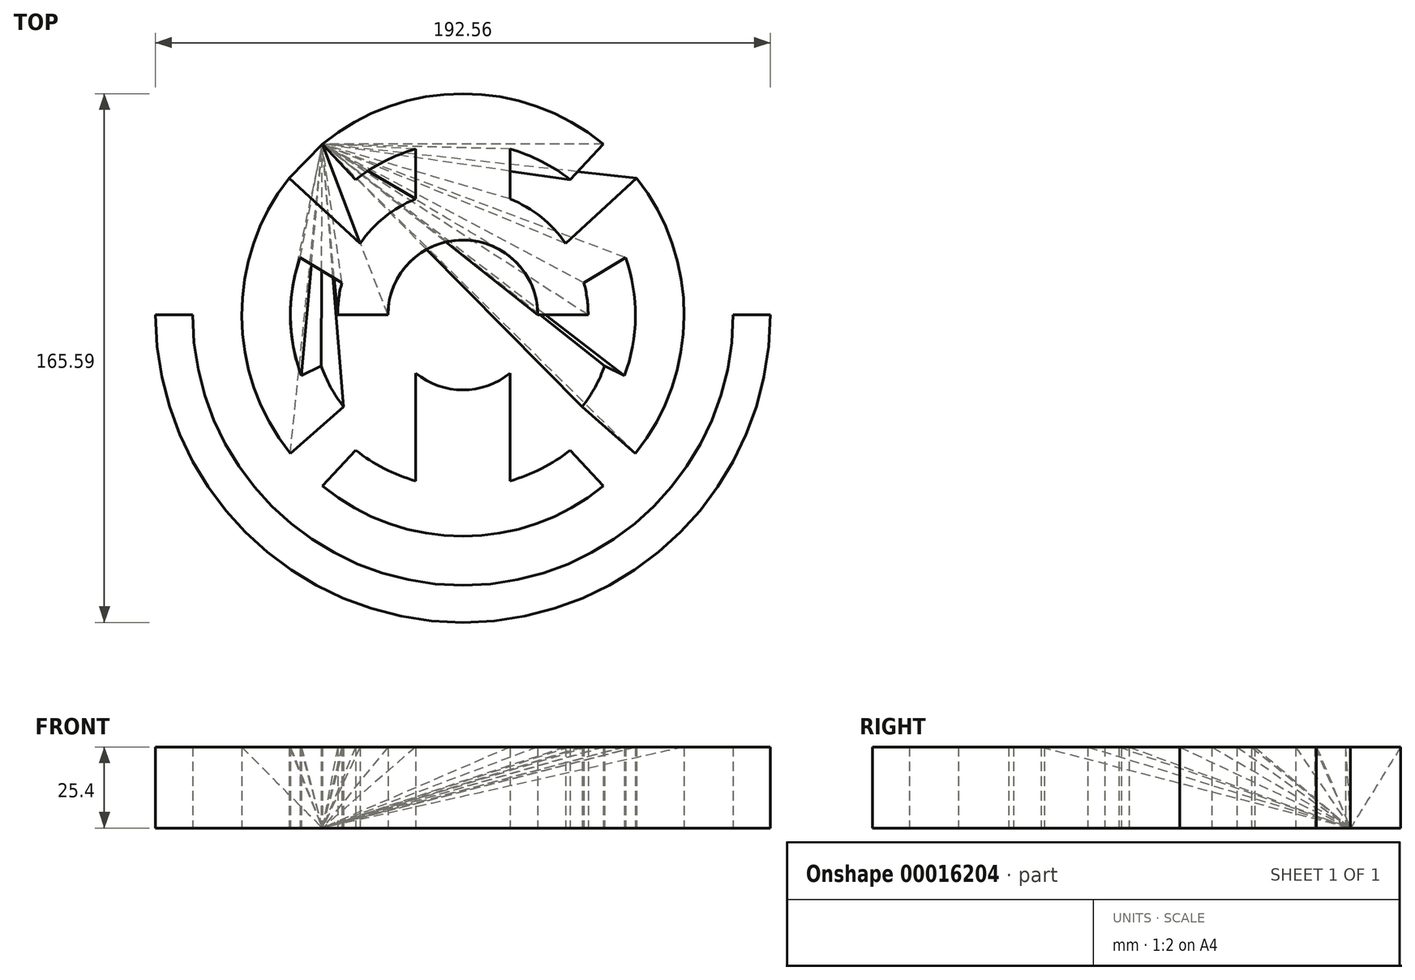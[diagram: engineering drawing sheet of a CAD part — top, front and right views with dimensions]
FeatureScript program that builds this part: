
annotation { "Feature Type Name" : "Feature", "Feature Type Description" : "" }
export const myFeature = defineFeature(function(context is Context, id is Id, definition is map)
    precondition{}
    {
        {
            var Q0;
            Q0=qCreatedBy(makeId("Top.planeOp"),FACE);
            var sketch = newSketch(context, id + "F0", { "sketchPlane" : qUnion([Q0])});
            skCircle(sketch, "E0", {"center": v(0, 0) * mm, "radius": 96.28 * mm});
            skCircle(sketch, "E1", {"center": v(0, 0) * mm, "radius": 84.65 * mm});
            skCircle(sketch, "E2", {"center": v(0, 0) * mm, "radius": 23.48 * mm});
            skCircle(sketch, "E3", {"center": v(0, 0) * mm, "radius": 39.24 * mm});
            skCircle(sketch, "E4", {"center": v(0, 0) * mm, "radius": 69.3 * mm});
            skCircle(sketch, "E5", {"center": v(0, 0) * mm, "radius": 54.05 * mm});
            skLineSegment(sketch, "E6", {"start": v(14.83, 67.7) * mm, "end": v(14.83, -51.98) * mm});
            skLineSegment(sketch, "E7", {"start": v(0, 69.3) * mm, "end": v(0, -96.28) * mm});
            skLineSegment(sketch, "E8.MirrorCS", {"start": v(-14.83, 67.7) * mm, "end": v(-14.83, -51.98) * mm});
            skLineSegment(sketch, "E9", {"start": v(96.28, 0) * mm, "end": v(-96.28, 0) * mm});
            skLineSegment(sketch, "E10", {"start": v(33.56, -42.37) * mm, "end": v(44.04, -53.52) * mm});
            skLineSegment(sketch, "E11.MirrorCS", {"start": v(-33.56, -42.37) * mm, "end": v(-44.04, -53.52) * mm});
            skLineSegment(sketch, "E12.MirrorCS", {"start": v(33.56, 42.37) * mm, "end": v(44.04, 53.52) * mm});
            skLineSegment(sketch, "E13.MirrorCS", {"start": v(-33.56, 42.37) * mm, "end": v(-44.04, 53.52) * mm});
            skCircle(sketch, "E14", {"center": v(0, 0) * mm, "radius": 47.19 * mm});
            skLineSegment(sketch, "E15", {"start": v(32.19, 22.45) * mm, "end": v(54.44, 42.9) * mm});
            skLineSegment(sketch, "E16", {"start": v(54.08, -43.34) * mm, "end": v(37.38, -28.8) * mm});
            skLineSegment(sketch, "E17", {"start": v(64.28, -25.92) * mm, "end": v(44.43, -15.9) * mm});
            skLineSegment(sketch, "E18", {"start": v(37.92, 10.11) * mm, "end": v(64.25, 25.99) * mm});
            skLineSegment(sketch, "E19.MirrorCS", {"start": v(-32.19, 22.45) * mm, "end": v(-54.44, 42.9) * mm});
            skLineSegment(sketch, "E20.MirrorCS", {"start": v(-37.92, 10.11) * mm, "end": v(-64.25, 25.99) * mm});
            skLineSegment(sketch, "E21.MirrorCS", {"start": v(-64.28, -25.92) * mm, "end": v(-44.43, -15.9) * mm});
            skLineSegment(sketch, "E22.MirrorCS", {"start": v(-54.08, -43.34) * mm, "end": v(-37.38, -28.8) * mm});
            skSolve(sketch);
        }
        {
            var Q0;
            {var subQ3=sQuery(id+"F0.wireOp",EDGE,"E3");var subQ5=sQuery(id+"F0.wireOp",EDGE,"E15");var subQ7=makeQuery(id+"F0.imprint","INTERSECT",VERTEX,{"derivedFrom":[subQ3,subQ5]});Q0=makeQuery(id+"F0.imprint","IMPRINT",FACE,{"disambiguationData":[TD([[makeQuery(id+"F0.imprint","IMPRINT",EDGE,{"disambiguationData":[TD([[subQ7,1.0]])],"derivedFrom":subQ3}),-1.0]])]});}
            var Q1;
            {var subQ3=sQuery(id+"F0.wireOp",EDGE,"E2");var subQ5=sQuery(id+"F0.wireOp",EDGE,"E6");var subQ7=makeQuery(id+"F0.imprint","INTERSECT",VERTEX,{"disambiguationData":[OD(0.0)],"derivedFrom":[subQ3,subQ5]});Q1=makeQuery(id+"F0.imprint","IMPRINT",FACE,{"disambiguationData":[TD([[makeQuery(id+"F0.imprint","IMPRINT",EDGE,{"disambiguationData":[TD([[subQ7,-1.0]])],"derivedFrom":subQ3}),-1.0]])]});}
            var Q2;
            {var subQ3=sQuery(id+"F0.wireOp",EDGE,"E4");var subQ5=sQuery(id+"F0.wireOp",EDGE,"E6");var subQ7=makeQuery(id+"F0.imprint","INTERSECT",VERTEX,{"derivedFrom":[subQ3,subQ5]});Q2=makeQuery(id+"F0.imprint","IMPRINT",FACE,{"disambiguationData":[TD([[makeQuery(id+"F0.imprint","IMPRINT",EDGE,{"disambiguationData":[TD([[subQ7,-1.0]])],"derivedFrom":subQ3}),1.0]])]});}
            var Q3;
            {var subQ0=sQuery(id+"F0.wireOp",EDGE,"E18");var subQ3=sQuery(id+"F0.wireOp",EDGE,"E4");var subQ4=makeQuery(id+"F0.imprint","INTERSECT",VERTEX,{"derivedFrom":[subQ3,subQ0]});Q3=makeQuery(id+"F0.imprint","IMPRINT",FACE,{"disambiguationData":[TD([[makeQuery(id+"F0.imprint","IMPRINT",EDGE,{"disambiguationData":[TD([[subQ4,1.0]])],"derivedFrom":subQ3}),1.0]])]});}
            var Q4;
            {var subQ0=sQuery(id+"F0.wireOp",EDGE,"E11.MirrorCS");Q4=makeQuery(id+"F0.imprint","IMPRINT",FACE,{"disambiguationData":[TD([[makeQuery(id+"F0.imprint","IMPRINT",EDGE,{"derivedFrom":subQ0}),1.0]])]});}
            var Q5;
            {var subQ3=sQuery(id+"F0.wireOp",EDGE,"E7");var subQ5=sQuery(id+"F0.wireOp",EDGE,"E5");var subQ7=makeQuery(id+"F0.imprint","INTERSECT",VERTEX,{"disambiguationData":[OD(0.0)],"derivedFrom":[subQ5,subQ3]});Q5=makeQuery(id+"F0.imprint","IMPRINT",FACE,{"disambiguationData":[TD([[makeQuery(id+"F0.imprint","IMPRINT",EDGE,{"disambiguationData":[TD([[subQ7,-1.0]])],"derivedFrom":subQ5}),1.0]])]});}
            var Q6;
            {var subQ3=sQuery(id+"F0.wireOp",EDGE,"E2");var subQ5=sQuery(id+"F0.wireOp",EDGE,"E7");var subQ7=makeQuery(id+"F0.imprint","INTERSECT",VERTEX,{"disambiguationData":[OD(1.0)],"derivedFrom":[subQ3,subQ5]});Q6=makeQuery(id+"F0.imprint","IMPRINT",FACE,{"disambiguationData":[TD([[makeQuery(id+"F0.imprint","IMPRINT",EDGE,{"disambiguationData":[TD([[subQ7,-1.0]])],"derivedFrom":subQ3}),-1.0]])]});}
            var Q7;
            {var subQ0=sQuery(id+"F0.wireOp",EDGE,"E8.MirrorCS");var subQ3=sQuery(id+"F0.wireOp",EDGE,"E2");var subQ4=makeQuery(id+"F0.imprint","INTERSECT",VERTEX,{"disambiguationData":[OD(1.0)],"derivedFrom":[subQ3,subQ0]});Q7=makeQuery(id+"F0.imprint","IMPRINT",FACE,{"disambiguationData":[TD([[makeQuery(id+"F0.imprint","IMPRINT",EDGE,{"disambiguationData":[TD([[subQ4,-1.0]])],"derivedFrom":subQ3}),-1.0]])]});}
            var Q8;
            {var subQ0=sQuery(id+"F0.wireOp",EDGE,"E12.MirrorCS");Q8=makeQuery(id+"F0.imprint","IMPRINT",FACE,{"disambiguationData":[TD([[makeQuery(id+"F0.imprint","IMPRINT",EDGE,{"derivedFrom":subQ0}),1.0]])]});}
            var Q9;
            {var subQ3=sQuery(id+"F0.wireOp",EDGE,"E4");var subQ5=sQuery(id+"F0.wireOp",EDGE,"E7");var subQ7=makeQuery(id+"F0.imprint","INTERSECT",VERTEX,{"disambiguationData":[OD(0.0)],"derivedFrom":[subQ3,subQ5]});Q9=makeQuery(id+"F0.imprint","IMPRINT",FACE,{"disambiguationData":[TD([[makeQuery(id+"F0.imprint","IMPRINT",EDGE,{"disambiguationData":[TD([[subQ7,-1.0]])],"derivedFrom":subQ3}),1.0]])]});}
            var Q10;
            {var subQ3=sQuery(id+"F0.wireOp",EDGE,"E4");var subQ5=sQuery(id+"F0.wireOp",EDGE,"E16");var subQ7=makeQuery(id+"F0.imprint","INTERSECT",VERTEX,{"derivedFrom":[subQ3,subQ5]});Q10=makeQuery(id+"F0.imprint","IMPRINT",FACE,{"disambiguationData":[TD([[makeQuery(id+"F0.imprint","IMPRINT",EDGE,{"disambiguationData":[TD([[subQ7,-1.0]])],"derivedFrom":subQ3}),1.0]])]});}
            var Q11;
            {var subQ0=sQuery(id+"F0.wireOp",EDGE,"E17");var subQ3=sQuery(id+"F0.wireOp",EDGE,"E4");var subQ4=makeQuery(id+"F0.imprint","INTERSECT",VERTEX,{"derivedFrom":[subQ3,subQ0]});Q11=makeQuery(id+"F0.imprint","IMPRINT",FACE,{"disambiguationData":[TD([[makeQuery(id+"F0.imprint","IMPRINT",EDGE,{"disambiguationData":[TD([[subQ4,-1.0]])],"derivedFrom":subQ3}),1.0]])]});}
            var Q12;
            {var subQ3=sQuery(id+"F0.wireOp",EDGE,"E0");var subQ5=sQuery(id+"F0.wireOp",EDGE,"E7");var subQ7=makeQuery(id+"F0.imprint","INTERSECT",VERTEX,{"derivedFrom":[subQ3,subQ5]});Q12=makeQuery(id+"F0.imprint","IMPRINT",FACE,{"disambiguationData":[TD([[makeQuery(id+"F0.imprint","IMPRINT",EDGE,{"disambiguationData":[TD([[subQ7,-1.0]])],"derivedFrom":subQ3}),1.0]])]});}
            var Q13;
            {var subQ0=sQuery(id+"F0.wireOp",EDGE,"E20.MirrorCS");var subQ3=sQuery(id+"F0.wireOp",EDGE,"E4");var subQ4=makeQuery(id+"F0.imprint","INTERSECT",VERTEX,{"derivedFrom":[subQ3,subQ0]});Q13=makeQuery(id+"F0.imprint","IMPRINT",FACE,{"disambiguationData":[TD([[makeQuery(id+"F0.imprint","IMPRINT",EDGE,{"disambiguationData":[TD([[subQ4,-1.0]])],"derivedFrom":subQ3}),1.0]])]});}
            var Q14;
            {var subQ3=sQuery(id+"F0.wireOp",EDGE,"E4");var subQ5=sQuery(id+"F0.wireOp",EDGE,"E21.MirrorCS");var subQ7=makeQuery(id+"F0.imprint","INTERSECT",VERTEX,{"derivedFrom":[subQ3,subQ5]});Q14=makeQuery(id+"F0.imprint","IMPRINT",FACE,{"disambiguationData":[TD([[makeQuery(id+"F0.imprint","IMPRINT",EDGE,{"disambiguationData":[TD([[subQ7,-1.0]])],"derivedFrom":subQ3}),1.0]])]});}
            var Q15;
            {var subQ3=sQuery(id+"F0.wireOp",EDGE,"E0");var subQ5=sQuery(id+"F0.wireOp",EDGE,"E7");var subQ7=makeQuery(id+"F0.imprint","INTERSECT",VERTEX,{"derivedFrom":[subQ3,subQ5]});Q15=makeQuery(id+"F0.imprint","IMPRINT",FACE,{"disambiguationData":[TD([[makeQuery(id+"F0.imprint","IMPRINT",EDGE,{"disambiguationData":[TD([[subQ7,1.0]])],"derivedFrom":subQ3}),1.0]])]});}
            var Q16;
            {var subQ1=sQuery(id+"F0.wireOp",EDGE,"E5");var subQ5=sQuery(id+"F0.wireOp",EDGE,"E16");var subQ6=makeQuery(id+"F0.imprint","INTERSECT",VERTEX,{"derivedFrom":[subQ1,subQ5]});Q16=makeQuery(id+"F0.imprint","IMPRINT",FACE,{"disambiguationData":[TD([[makeQuery(id+"F0.imprint","IMPRINT",EDGE,{"disambiguationData":[TD([[subQ6,-1.0]])],"derivedFrom":subQ1}),1.0]])]});}
            var Q17;
            {var subQ3=sQuery(id+"F0.wireOp",EDGE,"E4");var subQ5=sQuery(id+"F0.wireOp",EDGE,"E15");var subQ7=makeQuery(id+"F0.imprint","INTERSECT",VERTEX,{"derivedFrom":[subQ3,subQ5]});Q17=makeQuery(id+"F0.imprint","IMPRINT",FACE,{"disambiguationData":[TD([[makeQuery(id+"F0.imprint","IMPRINT",EDGE,{"disambiguationData":[TD([[subQ7,1.0]])],"derivedFrom":subQ3}),1.0]])]});}
            var Q18;
            {var subQ3=sQuery(id+"F0.wireOp",EDGE,"E7");var subQ5=sQuery(id+"F0.wireOp",EDGE,"E3");var subQ7=makeQuery(id+"F0.imprint","INTERSECT",VERTEX,{"disambiguationData":[OD(0.0)],"derivedFrom":[subQ5,subQ3]});Q18=makeQuery(id+"F0.imprint","IMPRINT",FACE,{"disambiguationData":[TD([[makeQuery(id+"F0.imprint","IMPRINT",EDGE,{"disambiguationData":[TD([[subQ7,-1.0]])],"derivedFrom":subQ5}),-1.0]])]});}
            var Q19;
            {var subQ0=sQuery(id+"F0.wireOp",EDGE,"E19.MirrorCS");var subQ3=sQuery(id+"F0.wireOp",EDGE,"E4");var subQ4=makeQuery(id+"F0.imprint","INTERSECT",VERTEX,{"derivedFrom":[subQ3,subQ0]});Q19=makeQuery(id+"F0.imprint","IMPRINT",FACE,{"disambiguationData":[TD([[makeQuery(id+"F0.imprint","IMPRINT",EDGE,{"disambiguationData":[TD([[subQ4,-1.0]])],"derivedFrom":subQ3}),1.0]])]});}
            var Q20;
            {var subQ1=sQuery(id+"F0.wireOp",EDGE,"E8.MirrorCS");var subQ5=sQuery(id+"F0.wireOp",EDGE,"E5");var subQ6=makeQuery(id+"F0.imprint","INTERSECT",VERTEX,{"disambiguationData":[OD(0.0)],"derivedFrom":[subQ5,subQ1]});Q20=makeQuery(id+"F0.imprint","IMPRINT",FACE,{"disambiguationData":[TD([[makeQuery(id+"F0.imprint","IMPRINT",EDGE,{"disambiguationData":[TD([[subQ6,-1.0]])],"derivedFrom":subQ5}),1.0]])]});}
            var Q21;
            {var subQ0=sQuery(id+"F0.wireOp",EDGE,"E21.MirrorCS");var subQ3=sQuery(id+"F0.wireOp",EDGE,"E4");var subQ4=makeQuery(id+"F0.imprint","INTERSECT",VERTEX,{"derivedFrom":[subQ3,subQ0]});Q21=makeQuery(id+"F0.imprint","IMPRINT",FACE,{"disambiguationData":[TD([[makeQuery(id+"F0.imprint","IMPRINT",EDGE,{"disambiguationData":[TD([[subQ4,1.0]])],"derivedFrom":subQ3}),1.0]])]});}
            var Q22;
            {var subQ0=sQuery(id+"F0.wireOp",EDGE,"E9");var subQ3=sQuery(id+"F0.wireOp",EDGE,"E2");var subQ4=makeQuery(id+"F0.imprint","INTERSECT",VERTEX,{"disambiguationData":[OD(1.0)],"derivedFrom":[subQ3,subQ0]});Q22=makeQuery(id+"F0.imprint","IMPRINT",FACE,{"disambiguationData":[TD([[makeQuery(id+"F0.imprint","IMPRINT",EDGE,{"disambiguationData":[TD([[subQ4,-1.0]])],"derivedFrom":subQ3}),-1.0]])]});}
            var Q23;
            {var subQ1=sQuery(id+"F0.wireOp",EDGE,"E8.MirrorCS");var subQ5=sQuery(id+"F0.wireOp",EDGE,"E3");var subQ6=makeQuery(id+"F0.imprint","INTERSECT",VERTEX,{"disambiguationData":[OD(1.0)],"derivedFrom":[subQ5,subQ1]});Q23=makeQuery(id+"F0.imprint","IMPRINT",FACE,{"disambiguationData":[TD([[makeQuery(id+"F0.imprint","IMPRINT",EDGE,{"disambiguationData":[TD([[subQ6,-1.0]])],"derivedFrom":subQ5}),-1.0]])]});}
            var Q24;
            {var subQ0=sQuery(id+"F0.wireOp",EDGE,"E6");var subQ3=sQuery(id+"F0.wireOp",EDGE,"E2");var subQ4=makeQuery(id+"F0.imprint","INTERSECT",VERTEX,{"disambiguationData":[OD(0.0)],"derivedFrom":[subQ3,subQ0]});Q24=makeQuery(id+"F0.imprint","IMPRINT",FACE,{"disambiguationData":[TD([[makeQuery(id+"F0.imprint","IMPRINT",EDGE,{"disambiguationData":[TD([[subQ4,1.0]])],"derivedFrom":subQ3}),-1.0]])]});}
            var Q25;
            {var subQ3=sQuery(id+"F0.wireOp",EDGE,"E6");var subQ5=sQuery(id+"F0.wireOp",EDGE,"E5");var subQ7=makeQuery(id+"F0.imprint","INTERSECT",VERTEX,{"disambiguationData":[OD(1.0)],"derivedFrom":[subQ5,subQ3]});Q25=makeQuery(id+"F0.imprint","IMPRINT",FACE,{"disambiguationData":[TD([[makeQuery(id+"F0.imprint","IMPRINT",EDGE,{"disambiguationData":[TD([[subQ7,-1.0]])],"derivedFrom":subQ5}),1.0]])]});}
            var Q26;
            {var subQ0=sQuery(id+"F0.wireOp",EDGE,"E18");var subQ3=sQuery(id+"F0.wireOp",EDGE,"E5");var subQ4=makeQuery(id+"F0.imprint","INTERSECT",VERTEX,{"derivedFrom":[subQ3,subQ0]});Q26=makeQuery(id+"F0.imprint","IMPRINT",FACE,{"disambiguationData":[TD([[makeQuery(id+"F0.imprint","IMPRINT",EDGE,{"disambiguationData":[TD([[subQ4,-1.0]])],"derivedFrom":subQ3}),1.0]])]});}
            var Q27;
            {var subQ0=sQuery(id+"F0.wireOp",EDGE,"E9");var subQ3=sQuery(id+"F0.wireOp",EDGE,"E0");var subQ6=makeQuery(id+"F0.imprint","INTERSECT",VERTEX,{"disambiguationData":[OD(0.0)],"derivedFrom":[subQ3,subQ0]});Q27=makeQuery(id+"F0.imprint","IMPRINT",FACE,{"disambiguationData":[TD([[makeQuery(id+"F0.imprint","IMPRINT",EDGE,{"disambiguationData":[TD([[subQ6,-1.0]])],"derivedFrom":subQ3}),1.0]])]});}
            var Q28;
            {var subQ0=sQuery(id+"F0.wireOp",EDGE,"E9");var subQ3=sQuery(id+"F0.wireOp",EDGE,"E2");var subQ4=makeQuery(id+"F0.imprint","INTERSECT",VERTEX,{"disambiguationData":[OD(0.0)],"derivedFrom":[subQ3,subQ0]});Q28=makeQuery(id+"F0.imprint","IMPRINT",FACE,{"disambiguationData":[TD([[makeQuery(id+"F0.imprint","IMPRINT",EDGE,{"disambiguationData":[TD([[subQ4,1.0]])],"derivedFrom":subQ3}),-1.0]])]});}
            var Q29;
            {var subQ1=sQuery(id+"F0.wireOp",EDGE,"E5");var subQ5=sQuery(id+"F0.wireOp",EDGE,"E21.MirrorCS");var subQ6=makeQuery(id+"F0.imprint","INTERSECT",VERTEX,{"derivedFrom":[subQ1,subQ5]});Q29=makeQuery(id+"F0.imprint","IMPRINT",FACE,{"disambiguationData":[TD([[makeQuery(id+"F0.imprint","IMPRINT",EDGE,{"disambiguationData":[TD([[subQ6,-1.0]])],"derivedFrom":subQ1}),1.0]])]});}
            var Q30;
            {var subQ3=sQuery(id+"F0.wireOp",EDGE,"E5");var subQ5=sQuery(id+"F0.wireOp",EDGE,"E19.MirrorCS");var subQ7=makeQuery(id+"F0.imprint","INTERSECT",VERTEX,{"derivedFrom":[subQ3,subQ5]});Q30=makeQuery(id+"F0.imprint","IMPRINT",FACE,{"disambiguationData":[TD([[makeQuery(id+"F0.imprint","IMPRINT",EDGE,{"disambiguationData":[TD([[subQ7,-1.0]])],"derivedFrom":subQ3}),1.0]])]});}
            var Q31;
            {var subQ3=sQuery(id+"F0.wireOp",EDGE,"E2");var subQ5=sQuery(id+"F0.wireOp",EDGE,"E8.MirrorCS");var subQ7=makeQuery(id+"F0.imprint","INTERSECT",VERTEX,{"disambiguationData":[OD(0.0)],"derivedFrom":[subQ3,subQ5]});Q31=makeQuery(id+"F0.imprint","IMPRINT",FACE,{"disambiguationData":[TD([[makeQuery(id+"F0.imprint","IMPRINT",EDGE,{"disambiguationData":[TD([[subQ7,-1.0]])],"derivedFrom":subQ3}),-1.0]])]});}
            var Q32;
            {var subQ1=sQuery(id+"F0.wireOp",EDGE,"E7");var subQ5=sQuery(id+"F0.wireOp",EDGE,"E3");var subQ6=makeQuery(id+"F0.imprint","INTERSECT",VERTEX,{"disambiguationData":[OD(1.0)],"derivedFrom":[subQ5,subQ1]});Q32=makeQuery(id+"F0.imprint","IMPRINT",FACE,{"disambiguationData":[TD([[makeQuery(id+"F0.imprint","IMPRINT",EDGE,{"disambiguationData":[TD([[subQ6,-1.0]])],"derivedFrom":subQ5}),-1.0]])]});}
            var Q33;
            {var subQ3=sQuery(id+"F0.wireOp",EDGE,"E6");var subQ5=sQuery(id+"F0.wireOp",EDGE,"E3");var subQ7=makeQuery(id+"F0.imprint","INTERSECT",VERTEX,{"disambiguationData":[OD(0.0)],"derivedFrom":[subQ5,subQ3]});Q33=makeQuery(id+"F0.imprint","IMPRINT",FACE,{"disambiguationData":[TD([[makeQuery(id+"F0.imprint","IMPRINT",EDGE,{"disambiguationData":[TD([[subQ7,-1.0]])],"derivedFrom":subQ5}),-1.0]])]});}
            var Q34;
            {var subQ3=sQuery(id+"F0.wireOp",EDGE,"E3");var subQ5=sQuery(id+"F0.wireOp",EDGE,"E19.MirrorCS");var subQ7=makeQuery(id+"F0.imprint","INTERSECT",VERTEX,{"derivedFrom":[subQ3,subQ5]});Q34=makeQuery(id+"F0.imprint","IMPRINT",FACE,{"disambiguationData":[TD([[makeQuery(id+"F0.imprint","IMPRINT",EDGE,{"disambiguationData":[TD([[subQ7,-1.0]])],"derivedFrom":subQ3}),-1.0]])]});}
            var Q35;
            {var subQ3=sQuery(id+"F0.wireOp",EDGE,"E6");var subQ5=sQuery(id+"F0.wireOp",EDGE,"E5");var subQ7=makeQuery(id+"F0.imprint","INTERSECT",VERTEX,{"disambiguationData":[OD(0.0)],"derivedFrom":[subQ5,subQ3]});Q35=makeQuery(id+"F0.imprint","IMPRINT",FACE,{"disambiguationData":[TD([[makeQuery(id+"F0.imprint","IMPRINT",EDGE,{"disambiguationData":[TD([[subQ7,1.0]])],"derivedFrom":subQ5}),1.0]])]});}
            var Q36;
            {var subQ0=sQuery(id+"F0.wireOp",EDGE,"E10");Q36=makeQuery(id+"F0.imprint","IMPRINT",FACE,{"disambiguationData":[TD([[makeQuery(id+"F0.imprint","IMPRINT",EDGE,{"derivedFrom":subQ0}),-1.0]])]});}
            var Q37;
            {var subQ3=sQuery(id+"F0.wireOp",EDGE,"E2");var subQ5=sQuery(id+"F0.wireOp",EDGE,"E7");var subQ7=makeQuery(id+"F0.imprint","INTERSECT",VERTEX,{"disambiguationData":[OD(0.0)],"derivedFrom":[subQ3,subQ5]});Q37=makeQuery(id+"F0.imprint","IMPRINT",FACE,{"disambiguationData":[TD([[makeQuery(id+"F0.imprint","IMPRINT",EDGE,{"disambiguationData":[TD([[subQ7,-1.0]])],"derivedFrom":subQ3}),-1.0]])]});}
            var Q38;
            {var subQ0=sQuery(id+"F0.wireOp",EDGE,"E13.MirrorCS");Q38=makeQuery(id+"F0.imprint","IMPRINT",FACE,{"disambiguationData":[TD([[makeQuery(id+"F0.imprint","IMPRINT",EDGE,{"derivedFrom":subQ0}),-1.0]])]});}
            extrude(context, id + "F1", {"entities" : qUnion([Q0, Q1, Q2, Q3, Q4, Q5, Q6, Q7, Q8, Q9, Q10, Q11, Q12, Q13, Q14, Q15, Q16, Q17, Q18, Q19, Q20, Q21, Q22, Q23, Q24, Q25, Q26, Q27, Q28, Q29, Q30, Q31, Q32, Q33, Q34, Q35, Q36, Q37, Q38]), "depth" : 25.4 * mm});
        }
        {
            var Q0;
            Q0=makeQuery(id+"F1.opExtrude","CAP_FACE",FACE,{"disambiguationData":[OSD([sQuery(id+"F0.wireOp",EDGE,"E2"),sQuery(id+"F0.wireOp",EDGE,"E3"),sQuery(id+"F0.wireOp",EDGE,"E4"),sQuery(id+"F0.wireOp",EDGE,"E5"),sQuery(id+"F0.wireOp",EDGE,"E6"),sQuery(id+"F0.wireOp",EDGE,"E8.MirrorCS"),sQuery(id+"F0.wireOp",EDGE,"E10"),sQuery(id+"F0.wireOp",EDGE,"E11.MirrorCS"),sQuery(id+"F0.wireOp",EDGE,"E12.MirrorCS"),sQuery(id+"F0.wireOp",EDGE,"E13.MirrorCS"),sQuery(id+"F0.wireOp",EDGE,"E14"),sQuery(id+"F0.wireOp",EDGE,"E15"),sQuery(id+"F0.wireOp",EDGE,"E16"),sQuery(id+"F0.wireOp",EDGE,"E17"),sQuery(id+"F0.wireOp",EDGE,"E18"),sQuery(id+"F0.wireOp",EDGE,"E19.MirrorCS"),sQuery(id+"F0.wireOp",EDGE,"E20.MirrorCS"),sQuery(id+"F0.wireOp",EDGE,"E21.MirrorCS"),sQuery(id+"F0.wireOp",EDGE,"E22.MirrorCS")])],"isStart":false});
            var Q1;
            Q1=makeQuery(id+"F1.opExtrude","CAP_VERTEX",VERTEX,{"disambiguationData":[OSD([sQuery(id+"F0.wireOp",EDGE,"E4"),sQuery(id+"F0.wireOp",EDGE,"E13.MirrorCS")])],"isStart":true});
            loft(context, id + "F2", {"sheetProfilesArray" : [{ "sheetProfileEntities" : qUnion([Q0]) }, { "sheetProfileEntities" : qUnion([Q1]) }]});
        }
    });
